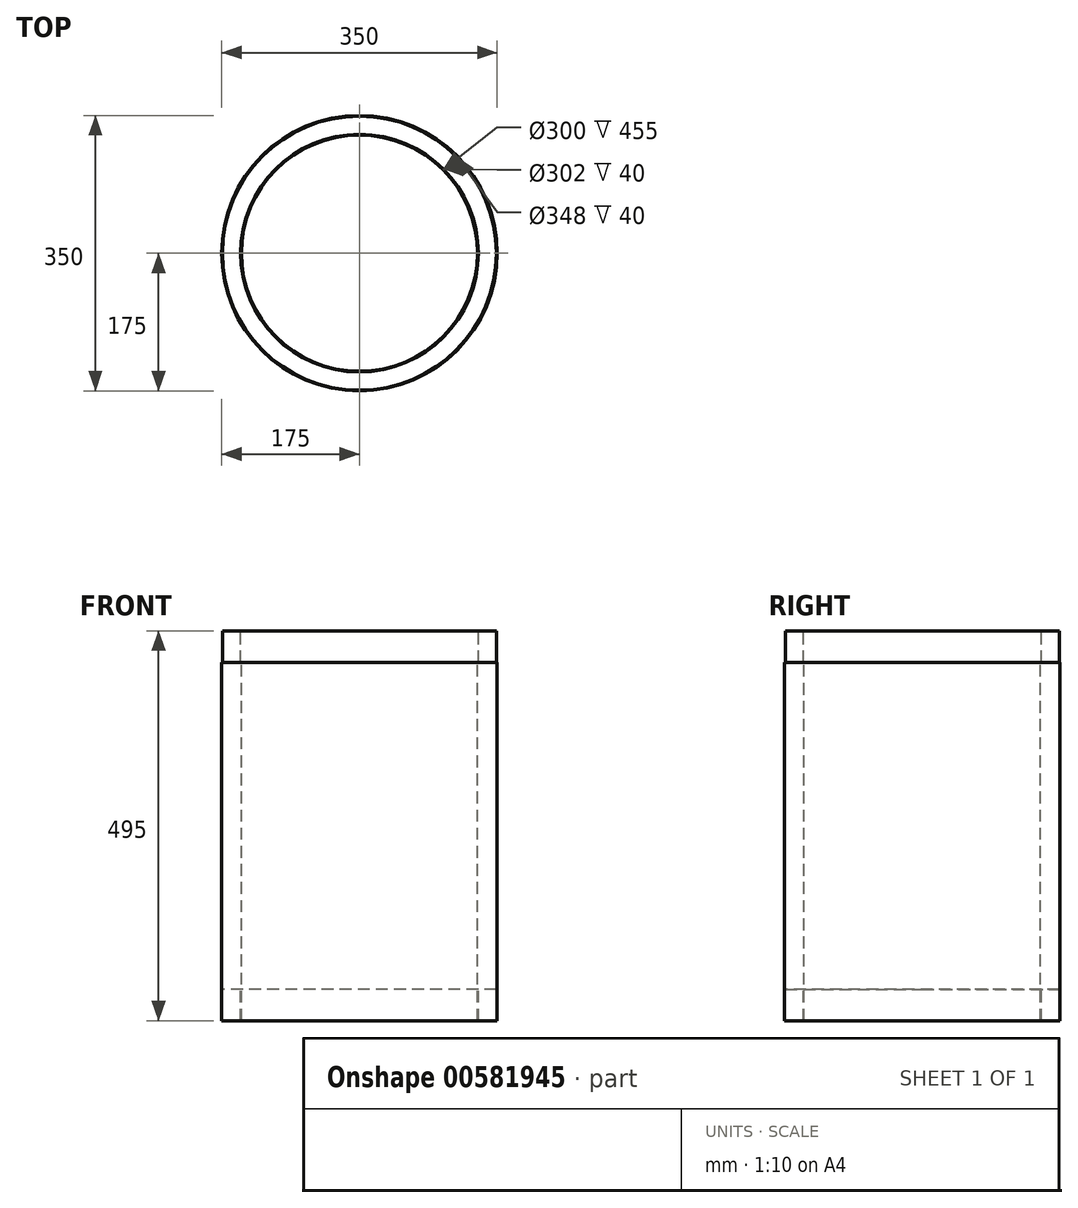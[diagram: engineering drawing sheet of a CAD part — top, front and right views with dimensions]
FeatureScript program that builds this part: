
annotation { "Feature Type Name" : "Feature", "Feature Type Description" : "" }
export const myFeature = defineFeature(function(context is Context, id is Id, definition is map)
    precondition{}
    {
        {
            var Q0;
            Q0=qCreatedBy(makeId("Front.planeOp"),FACE);
            var sketch = newSketch(context, id + "F0", { "sketchPlane" : qUnion([Q0])});
            skLineSegment(sketch, "E0", {"start": v(0, 345.75) * mm, "end": v(0, -558.03) * mm, "construction": true});
            skLineSegment(sketch, "E1", {"start": v(-150, -518.84) * mm, "end": v(-150, -63.84) * mm});
            skLineSegment(sketch, "E2", {"start": v(-150, -63.84) * mm, "end": v(-151, -63.84) * mm});
            skLineSegment(sketch, "E3", {"start": v(-151, -63.84) * mm, "end": v(-151, -23.84) * mm});
            skLineSegment(sketch, "E4", {"start": v(-151, -23.84) * mm, "end": v(-174, -23.84) * mm});
            skLineSegment(sketch, "E5", {"start": v(-174, -23.84) * mm, "end": v(-174, -63.84) * mm});
            skLineSegment(sketch, "E6", {"start": v(-174, -63.84) * mm, "end": v(-175, -63.84) * mm});
            skLineSegment(sketch, "E7", {"start": v(-175, -63.84) * mm, "end": v(-175, -518.84) * mm});
            skLineSegment(sketch, "E8", {"start": v(-175, -518.84) * mm, "end": v(-174, -518.84) * mm});
            skLineSegment(sketch, "E9", {"start": v(-174, -518.84) * mm, "end": v(-174, -478.84) * mm});
            skLineSegment(sketch, "E10", {"start": v(-174, -478.84) * mm, "end": v(-151, -478.84) * mm});
            skLineSegment(sketch, "E11", {"start": v(-151, -478.84) * mm, "end": v(-151, -518.84) * mm});
            skLineSegment(sketch, "E12", {"start": v(-151, -518.84) * mm, "end": v(-150, -518.84) * mm});
            skSolve(sketch);
        }
        {
            var Q0;
            Q0=qSketchRegion(id+"F0",true);
            var Q1;
            Q1=sQuery(id+"F0.wireOp",EDGE,"E0");
            revolve(context, id + "F1", {"entities" : qUnion([Q0]), "axis" : qUnion([Q1]), "revolveType" : RevolveType.FULL});
        }
    });
